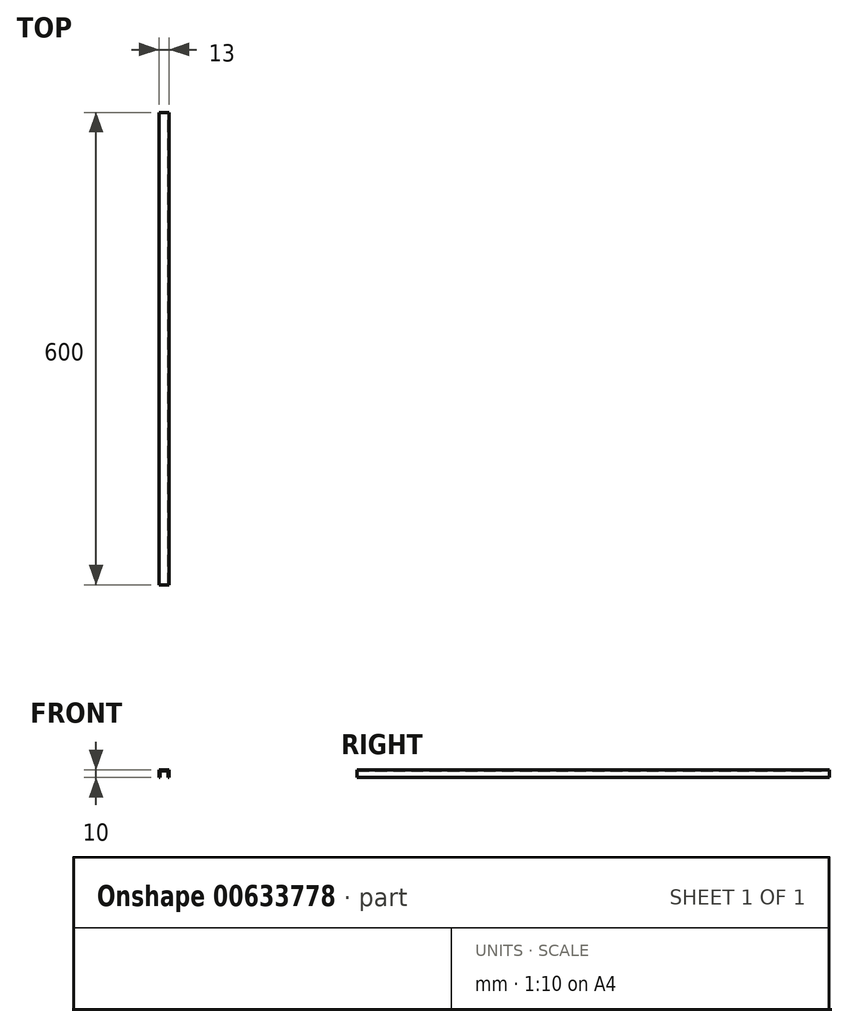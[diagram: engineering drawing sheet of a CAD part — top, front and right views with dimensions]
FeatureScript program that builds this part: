
annotation { "Feature Type Name" : "Feature", "Feature Type Description" : "" }
export const myFeature = defineFeature(function(context is Context, id is Id, definition is map)
    precondition{}
    {
        {
            var Q0;
            Q0=qCreatedBy(makeId("Front.planeOp"),FACE);
            var sketch = newSketch(context, id + "F0", { "sketchPlane" : qUnion([Q0])});
            skLineSegment(sketch, "E0.bottom", {"start": v(3.26, 0.03) * mm, "end": v(16.26, 0.03) * mm});
            skLineSegment(sketch, "E0.left", {"start": v(3.26, 0.03) * mm, "end": v(3.26, -9.97) * mm});
            skLineSegment(sketch, "E0.right", {"start": v(16.26, 0.03) * mm, "end": v(16.26, -9.97) * mm});
            skLineSegment(sketch, "E1.0", {"start": v(4.76, -1.47) * mm, "end": v(4.76, -9.97) * mm});
            skLineSegment(sketch, "E1.1", {"start": v(4.76, -1.47) * mm, "end": v(14.76, -1.47) * mm});
            skLineSegment(sketch, "E1.2", {"start": v(14.76, -1.47) * mm, "end": v(14.76, -9.97) * mm});
            skLineSegment(sketch, "E2", {"start": v(3.26, -9.97) * mm, "end": v(4.76, -9.97) * mm});
            skLineSegment(sketch, "E3", {"start": v(14.76, -9.97) * mm, "end": v(16.26, -9.97) * mm});
            skSolve(sketch);
        }
        {
            var Q0;
            Q0=makeQuery(id+"F0.imprint","IMPRINT",FACE,{"disambiguationData":[TD([[makeQuery(id+"F0.imprint","IMPRINT",EDGE,{"derivedFrom":sQuery(id+"F0.wireOp",EDGE,"E0.bottom")}),-1.0]])]});
            extrude(context, id + "F1", {"entities" : qUnion([Q0]), "depth" : 600 * mm, "offsetDistance" : 25 * mm});
        }
    });
